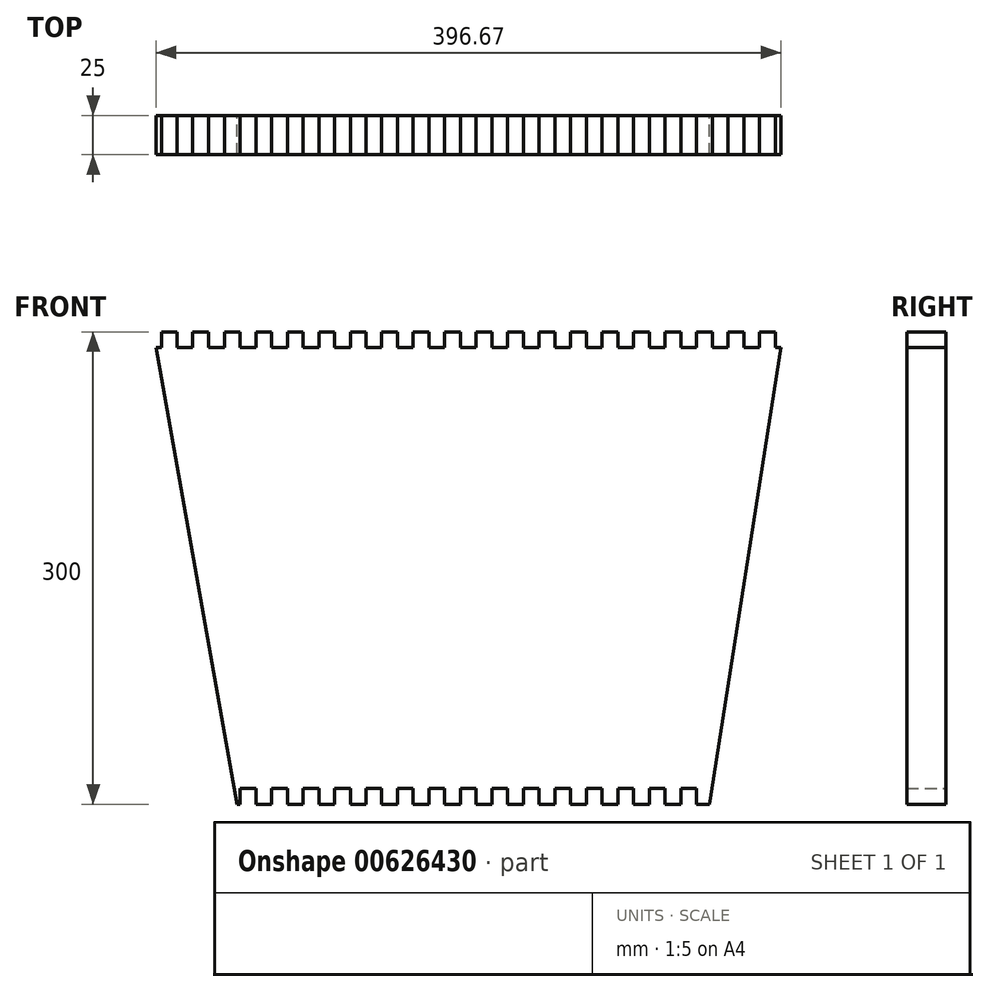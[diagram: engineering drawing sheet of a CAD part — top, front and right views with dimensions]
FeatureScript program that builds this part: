
annotation { "Feature Type Name" : "Feature", "Feature Type Description" : "" }
export const myFeature = defineFeature(function(context is Context, id is Id, definition is map)
    precondition{}
    {
        {
            var Q0;
            Q0=qCreatedBy(makeId("Front.planeOp"),FACE);
            var sketch = newSketch(context, id + "F0", { "sketchPlane" : qUnion([Q0])});
            skLineSegment(sketch, "E0.top", {"start": v(200, 150) * mm, "end": v(-200, 150) * mm});
            skPoint(sketch, "E0.middle", {"position": v(0, 0) * mm});
            skLineSegment(sketch, "E1.bottom", {"start": v(153.17, -150) * mm, "end": v(-146.83, -150) * mm});
            skLineSegment(sketch, "E2", {"start": v(-200, 150) * mm, "end": v(-146.83, -150) * mm});
            skLineSegment(sketch, "E3", {"start": v(153.17, -150) * mm, "end": v(200, 150) * mm});
            skLineSegment(sketch, "E4", {"start": v(5, 150) * mm, "end": v(0, 150) * mm});
            skLineSegment(sketch, "E5.bottom", {"start": v(5, 150) * mm, "end": v(-5, 150) * mm});
            skLineSegment(sketch, "E5.top", {"start": v(5, 140) * mm, "end": v(-5, 140) * mm});
            skLineSegment(sketch, "E5.left", {"start": v(5, 150) * mm, "end": v(5, 140) * mm});
            skLineSegment(sketch, "E5.right", {"start": v(-5, 150) * mm, "end": v(-5, 140) * mm});
            skLineSegment(sketch, "E6.1.0.0", {"start": v(-25, 150) * mm, "end": v(-25, 140) * mm});
            skLineSegment(sketch, "E6.1.0.1", {"start": v(-15, 140) * mm, "end": v(-25, 140) * mm});
            skLineSegment(sketch, "E6.1.0.2", {"start": v(-15, 150) * mm, "end": v(-15, 140) * mm});
            skLineSegment(sketch, "E6.1.0.3", {"start": v(-15, 150) * mm, "end": v(-25, 150) * mm});
            skLineSegment(sketch, "E6.2.0.0", {"start": v(-45, 150) * mm, "end": v(-45, 140) * mm});
            skLineSegment(sketch, "E6.2.0.1", {"start": v(-35, 140) * mm, "end": v(-45, 140) * mm});
            skLineSegment(sketch, "E6.2.0.2", {"start": v(-35, 150) * mm, "end": v(-35, 140) * mm});
            skLineSegment(sketch, "E6.2.0.3", {"start": v(-35, 150) * mm, "end": v(-45, 150) * mm});
            skLineSegment(sketch, "E6.3.0.0", {"start": v(-65, 150) * mm, "end": v(-65, 140) * mm});
            skLineSegment(sketch, "E6.3.0.1", {"start": v(-55, 140) * mm, "end": v(-65, 140) * mm});
            skLineSegment(sketch, "E6.3.0.2", {"start": v(-55, 150) * mm, "end": v(-55, 140) * mm});
            skLineSegment(sketch, "E6.3.0.3", {"start": v(-55, 150) * mm, "end": v(-65, 150) * mm});
            skLineSegment(sketch, "E6.4.0.0", {"start": v(-85, 150) * mm, "end": v(-85, 140) * mm});
            skLineSegment(sketch, "E6.4.0.1", {"start": v(-75, 140) * mm, "end": v(-85, 140) * mm});
            skLineSegment(sketch, "E6.4.0.2", {"start": v(-75, 150) * mm, "end": v(-75, 140) * mm});
            skLineSegment(sketch, "E6.4.0.3", {"start": v(-75, 150) * mm, "end": v(-85, 150) * mm});
            skLineSegment(sketch, "E6.5.0.0", {"start": v(-105, 150) * mm, "end": v(-105, 140) * mm});
            skLineSegment(sketch, "E6.5.0.1", {"start": v(-95, 140) * mm, "end": v(-105, 140) * mm});
            skLineSegment(sketch, "E6.5.0.2", {"start": v(-95, 150) * mm, "end": v(-95, 140) * mm});
            skLineSegment(sketch, "E6.5.0.3", {"start": v(-95, 150) * mm, "end": v(-105, 150) * mm});
            skLineSegment(sketch, "E6.6.0.0", {"start": v(-125, 150) * mm, "end": v(-125, 140) * mm});
            skLineSegment(sketch, "E6.6.0.1", {"start": v(-115, 140) * mm, "end": v(-125, 140) * mm});
            skLineSegment(sketch, "E6.6.0.2", {"start": v(-115, 150) * mm, "end": v(-115, 140) * mm});
            skLineSegment(sketch, "E6.6.0.3", {"start": v(-115, 150) * mm, "end": v(-125, 150) * mm});
            skLineSegment(sketch, "E6.7.0.0", {"start": v(-145, 150) * mm, "end": v(-145, 140) * mm});
            skLineSegment(sketch, "E6.7.0.1", {"start": v(-135, 140) * mm, "end": v(-145, 140) * mm});
            skLineSegment(sketch, "E6.7.0.2", {"start": v(-135, 150) * mm, "end": v(-135, 140) * mm});
            skLineSegment(sketch, "E6.7.0.3", {"start": v(-135, 150) * mm, "end": v(-145, 150) * mm});
            skLineSegment(sketch, "E6.8.0.0", {"start": v(-165, 150) * mm, "end": v(-165, 140) * mm});
            skLineSegment(sketch, "E6.8.0.1", {"start": v(-155, 140) * mm, "end": v(-165, 140) * mm});
            skLineSegment(sketch, "E6.8.0.2", {"start": v(-155, 150) * mm, "end": v(-155, 140) * mm});
            skLineSegment(sketch, "E6.8.0.3", {"start": v(-155, 150) * mm, "end": v(-165, 150) * mm});
            skLineSegment(sketch, "E6.9.0.0", {"start": v(-185, 150) * mm, "end": v(-185, 140) * mm});
            skLineSegment(sketch, "E6.9.0.1", {"start": v(-175, 140) * mm, "end": v(-185, 140) * mm});
            skLineSegment(sketch, "E6.9.0.2", {"start": v(-175, 150) * mm, "end": v(-175, 140) * mm});
            skLineSegment(sketch, "E6.9.0.3", {"start": v(-175, 150) * mm, "end": v(-185, 150) * mm});
            skLineSegment(sketch, "E6.10.0.0", {"start": v(-205, 150) * mm, "end": v(-205, 140) * mm});
            skLineSegment(sketch, "E6.10.0.1", {"start": v(-195, 140) * mm, "end": v(-205, 140) * mm});
            skLineSegment(sketch, "E6.10.0.2", {"start": v(-195, 150) * mm, "end": v(-195, 140) * mm});
            skLineSegment(sketch, "E6.10.0.3", {"start": v(-195, 150) * mm, "end": v(-205, 150) * mm});
            skLineSegment(sketch, "E7.1.0.0", {"start": v(15, 150) * mm, "end": v(15, 140) * mm});
            skLineSegment(sketch, "E7.1.0.1", {"start": v(25, 140) * mm, "end": v(15, 140) * mm});
            skLineSegment(sketch, "E7.1.0.2", {"start": v(25, 150) * mm, "end": v(25, 140) * mm});
            skLineSegment(sketch, "E7.1.0.3", {"start": v(25, 150) * mm, "end": v(15, 150) * mm});
            skLineSegment(sketch, "E7.2.0.0", {"start": v(35, 150) * mm, "end": v(35, 140) * mm});
            skLineSegment(sketch, "E7.2.0.1", {"start": v(45, 140) * mm, "end": v(35, 140) * mm});
            skLineSegment(sketch, "E7.2.0.2", {"start": v(45, 150) * mm, "end": v(45, 140) * mm});
            skLineSegment(sketch, "E7.2.0.3", {"start": v(45, 150) * mm, "end": v(35, 150) * mm});
            skLineSegment(sketch, "E7.3.0.0", {"start": v(55, 150) * mm, "end": v(55, 140) * mm});
            skLineSegment(sketch, "E7.3.0.1", {"start": v(65, 140) * mm, "end": v(55, 140) * mm});
            skLineSegment(sketch, "E7.3.0.2", {"start": v(65, 150) * mm, "end": v(65, 140) * mm});
            skLineSegment(sketch, "E7.3.0.3", {"start": v(65, 150) * mm, "end": v(55, 150) * mm});
            skLineSegment(sketch, "E7.4.0.0", {"start": v(75, 150) * mm, "end": v(75, 140) * mm});
            skLineSegment(sketch, "E7.4.0.1", {"start": v(85, 140) * mm, "end": v(75, 140) * mm});
            skLineSegment(sketch, "E7.4.0.2", {"start": v(85, 150) * mm, "end": v(85, 140) * mm});
            skLineSegment(sketch, "E7.4.0.3", {"start": v(85, 150) * mm, "end": v(75, 150) * mm});
            skLineSegment(sketch, "E7.5.0.0", {"start": v(95, 150) * mm, "end": v(95, 140) * mm});
            skLineSegment(sketch, "E7.5.0.1", {"start": v(105, 140) * mm, "end": v(95, 140) * mm});
            skLineSegment(sketch, "E7.5.0.2", {"start": v(105, 150) * mm, "end": v(105, 140) * mm});
            skLineSegment(sketch, "E7.5.0.3", {"start": v(105, 150) * mm, "end": v(95, 150) * mm});
            skLineSegment(sketch, "E7.6.0.0", {"start": v(115, 150) * mm, "end": v(115, 140) * mm});
            skLineSegment(sketch, "E7.6.0.1", {"start": v(125, 140) * mm, "end": v(115, 140) * mm});
            skLineSegment(sketch, "E7.6.0.2", {"start": v(125, 150) * mm, "end": v(125, 140) * mm});
            skLineSegment(sketch, "E7.6.0.3", {"start": v(125, 150) * mm, "end": v(115, 150) * mm});
            skLineSegment(sketch, "E7.7.0.0", {"start": v(135, 150) * mm, "end": v(135, 140) * mm});
            skLineSegment(sketch, "E7.7.0.1", {"start": v(145, 140) * mm, "end": v(135, 140) * mm});
            skLineSegment(sketch, "E7.7.0.2", {"start": v(145, 150) * mm, "end": v(145, 140) * mm});
            skLineSegment(sketch, "E7.7.0.3", {"start": v(145, 150) * mm, "end": v(135, 150) * mm});
            skLineSegment(sketch, "E7.8.0.0", {"start": v(155, 150) * mm, "end": v(155, 140) * mm});
            skLineSegment(sketch, "E7.8.0.1", {"start": v(165, 140) * mm, "end": v(155, 140) * mm});
            skLineSegment(sketch, "E7.8.0.2", {"start": v(165, 150) * mm, "end": v(165, 140) * mm});
            skLineSegment(sketch, "E7.8.0.3", {"start": v(165, 150) * mm, "end": v(155, 150) * mm});
            skLineSegment(sketch, "E7.9.0.0", {"start": v(175, 150) * mm, "end": v(175, 140) * mm});
            skLineSegment(sketch, "E7.9.0.1", {"start": v(185, 140) * mm, "end": v(175, 140) * mm});
            skLineSegment(sketch, "E7.9.0.2", {"start": v(185, 150) * mm, "end": v(185, 140) * mm});
            skLineSegment(sketch, "E7.9.0.3", {"start": v(185, 150) * mm, "end": v(175, 150) * mm});
            skLineSegment(sketch, "E7.10.0.0", {"start": v(195, 150) * mm, "end": v(195, 140) * mm});
            skLineSegment(sketch, "E7.10.0.1", {"start": v(205, 140) * mm, "end": v(195, 140) * mm});
            skLineSegment(sketch, "E7.10.0.2", {"start": v(205, 150) * mm, "end": v(205, 140) * mm});
            skLineSegment(sketch, "E7.10.0.3", {"start": v(205, 150) * mm, "end": v(195, 150) * mm});
            skLineSegment(sketch, "E7.direction1", {"start": v(-5, 140) * mm, "end": v(15, 140) * mm, "construction": true});
            skLineSegment(sketch, "E8.MirrorCS", {"start": v(95, -150) * mm, "end": v(95, -140) * mm});
            skLineSegment(sketch, "E9.MirrorCS", {"start": v(15, -150) * mm, "end": v(15, -140) * mm});
            skLineSegment(sketch, "E10.MirrorCS", {"start": v(105, -140) * mm, "end": v(95, -140) * mm});
            skLineSegment(sketch, "E11.MirrorCS", {"start": v(25, -140) * mm, "end": v(15, -140) * mm});
            skLineSegment(sketch, "E12.MirrorCS", {"start": v(195, -150) * mm, "end": v(195, -140) * mm});
            skLineSegment(sketch, "E13.MirrorCS", {"start": v(45, -150) * mm, "end": v(45, -140) * mm});
            skLineSegment(sketch, "E14.MirrorCS", {"start": v(-155, -150) * mm, "end": v(-155, -140) * mm});
            skLineSegment(sketch, "E15.MirrorCS", {"start": v(-75, -150) * mm, "end": v(-75, -140) * mm});
            skLineSegment(sketch, "E16.MirrorCS", {"start": v(125, -150) * mm, "end": v(125, -140) * mm});
            skLineSegment(sketch, "E17.MirrorCS", {"start": v(-5, -150) * mm, "end": v(-5, -140) * mm});
            skLineSegment(sketch, "E18.MirrorCS", {"start": v(-45, -150) * mm, "end": v(-45, -140) * mm});
            skLineSegment(sketch, "E19.MirrorCS", {"start": v(-15, -150) * mm, "end": v(-25, -150) * mm});
            skLineSegment(sketch, "E20.MirrorCS", {"start": v(-125, -150) * mm, "end": v(-125, -140) * mm});
            skLineSegment(sketch, "E21.MirrorCS", {"start": v(5, -140) * mm, "end": v(-5, -140) * mm});
            skLineSegment(sketch, "E22.MirrorCS", {"start": v(-5, -140) * mm, "end": v(15, -140) * mm, "construction": true});
            skLineSegment(sketch, "E23.MirrorCS", {"start": v(155, -150) * mm, "end": v(155, -140) * mm});
            skLineSegment(sketch, "E24.MirrorCS", {"start": v(-185, -150) * mm, "end": v(-185, -140) * mm});
            skLineSegment(sketch, "E25.MirrorCS", {"start": v(5, -150) * mm, "end": v(0, -150) * mm});
            skLineSegment(sketch, "E26.MirrorCS", {"start": v(5, -150) * mm, "end": v(-5, -150) * mm});
            skLineSegment(sketch, "E27.MirrorCS", {"start": v(85, -150) * mm, "end": v(75, -150) * mm});
            skLineSegment(sketch, "E28.MirrorCS", {"start": v(-195, -150) * mm, "end": v(-205, -150) * mm});
            skLineSegment(sketch, "E29.MirrorCS", {"start": v(-115, -150) * mm, "end": v(-125, -150) * mm});
            skLineSegment(sketch, "E30.MirrorCS", {"start": v(-65, -150) * mm, "end": v(-65, -140) * mm});
            skLineSegment(sketch, "E31.MirrorCS", {"start": v(175, -150) * mm, "end": v(175, -140) * mm});
            skLineSegment(sketch, "E32.MirrorCS", {"start": v(-145, -150) * mm, "end": v(-145, -140) * mm});
            skLineSegment(sketch, "E33.MirrorCS", {"start": v(-55, -140) * mm, "end": v(-65, -140) * mm});
            skLineSegment(sketch, "E34.MirrorCS", {"start": v(185, -140) * mm, "end": v(175, -140) * mm});
            skLineSegment(sketch, "E35.MirrorCS", {"start": v(-135, -140) * mm, "end": v(-145, -140) * mm});
            skLineSegment(sketch, "E36.MirrorCS", {"start": v(-55, -150) * mm, "end": v(-55, -140) * mm});
            skLineSegment(sketch, "E37.MirrorCS", {"start": v(185, -150) * mm, "end": v(185, -140) * mm});
            skLineSegment(sketch, "E38.MirrorCS", {"start": v(105, -150) * mm, "end": v(105, -140) * mm});
            skLineSegment(sketch, "E39.MirrorCS", {"start": v(25, -150) * mm, "end": v(25, -140) * mm});
            skLineSegment(sketch, "E40.MirrorCS", {"start": v(-135, -150) * mm, "end": v(-135, -140) * mm});
            skLineSegment(sketch, "E41.MirrorCS", {"start": v(-55, -150) * mm, "end": v(-65, -150) * mm});
            skLineSegment(sketch, "E42.MirrorCS", {"start": v(185, -150) * mm, "end": v(175, -150) * mm});
            skLineSegment(sketch, "E43.MirrorCS", {"start": v(105, -150) * mm, "end": v(95, -150) * mm});
            skLineSegment(sketch, "E44.MirrorCS", {"start": v(25, -150) * mm, "end": v(15, -150) * mm});
            skLineSegment(sketch, "E45.MirrorCS", {"start": v(-135, -150) * mm, "end": v(-145, -150) * mm});
            skLineSegment(sketch, "E46.MirrorCS", {"start": v(35, -150) * mm, "end": v(35, -140) * mm});
            skLineSegment(sketch, "E47.MirrorCS", {"start": v(-165, -150) * mm, "end": v(-165, -140) * mm});
            skLineSegment(sketch, "E48.MirrorCS", {"start": v(-85, -150) * mm, "end": v(-85, -140) * mm});
            skLineSegment(sketch, "E49.MirrorCS", {"start": v(115, -150) * mm, "end": v(115, -140) * mm});
            skLineSegment(sketch, "E50.MirrorCS", {"start": v(45, -140) * mm, "end": v(35, -140) * mm});
            skLineSegment(sketch, "E51.MirrorCS", {"start": v(-155, -140) * mm, "end": v(-165, -140) * mm});
            skLineSegment(sketch, "E52.MirrorCS", {"start": v(-75, -140) * mm, "end": v(-85, -140) * mm});
            skLineSegment(sketch, "E53.MirrorCS", {"start": v(205, -140) * mm, "end": v(195, -140) * mm});
            skLineSegment(sketch, "E54.MirrorCS", {"start": v(125, -140) * mm, "end": v(115, -140) * mm});
            skLineSegment(sketch, "E55.MirrorCS", {"start": v(205, -150) * mm, "end": v(205, -140) * mm});
            skLineSegment(sketch, "E56.MirrorCS", {"start": v(45, -150) * mm, "end": v(35, -150) * mm});
            skLineSegment(sketch, "E57.MirrorCS", {"start": v(-75, -150) * mm, "end": v(-85, -150) * mm});
            skLineSegment(sketch, "E58.MirrorCS", {"start": v(-155, -150) * mm, "end": v(-165, -150) * mm});
            skLineSegment(sketch, "E59.MirrorCS", {"start": v(205, -150) * mm, "end": v(195, -150) * mm});
            skLineSegment(sketch, "E60.MirrorCS", {"start": v(125, -150) * mm, "end": v(115, -150) * mm});
            skLineSegment(sketch, "E61.MirrorCS", {"start": v(165, -150) * mm, "end": v(155, -150) * mm});
            skLineSegment(sketch, "E62.MirrorCS", {"start": v(-35, -150) * mm, "end": v(-45, -150) * mm});
            skLineSegment(sketch, "E63.MirrorCS", {"start": v(-95, -150) * mm, "end": v(-105, -150) * mm});
            skLineSegment(sketch, "E64.MirrorCS", {"start": v(-175, -150) * mm, "end": v(-185, -150) * mm});
            skLineSegment(sketch, "E65.MirrorCS", {"start": v(65, -150) * mm, "end": v(55, -150) * mm});
            skLineSegment(sketch, "E66.MirrorCS", {"start": v(-115, -150) * mm, "end": v(-115, -140) * mm});
            skLineSegment(sketch, "E67.MirrorCS", {"start": v(-195, -150) * mm, "end": v(-195, -140) * mm});
            skLineSegment(sketch, "E68.MirrorCS", {"start": v(85, -150) * mm, "end": v(85, -140) * mm});
            skLineSegment(sketch, "E69.MirrorCS", {"start": v(165, -150) * mm, "end": v(165, -140) * mm});
            skLineSegment(sketch, "E70.MirrorCS", {"start": v(145, -150) * mm, "end": v(135, -150) * mm});
            skLineSegment(sketch, "E71.MirrorCS", {"start": v(-35, -150) * mm, "end": v(-35, -140) * mm});
            skLineSegment(sketch, "E72.MirrorCS", {"start": v(145, -140) * mm, "end": v(135, -140) * mm});
            skLineSegment(sketch, "E73.MirrorCS", {"start": v(-95, -140) * mm, "end": v(-105, -140) * mm});
            skLineSegment(sketch, "E74.MirrorCS", {"start": v(-115, -140) * mm, "end": v(-125, -140) * mm});
            skLineSegment(sketch, "E75.MirrorCS", {"start": v(-195, -140) * mm, "end": v(-205, -140) * mm});
            skLineSegment(sketch, "E76.MirrorCS", {"start": v(85, -140) * mm, "end": v(75, -140) * mm});
            skLineSegment(sketch, "E77.MirrorCS", {"start": v(165, -140) * mm, "end": v(155, -140) * mm});
            skLineSegment(sketch, "E78.MirrorCS", {"start": v(-35, -140) * mm, "end": v(-45, -140) * mm});
            skLineSegment(sketch, "E79.MirrorCS", {"start": v(-15, -140) * mm, "end": v(-25, -140) * mm});
            skLineSegment(sketch, "E80.MirrorCS", {"start": v(-25, -150) * mm, "end": v(-25, -140) * mm});
            skLineSegment(sketch, "E81.MirrorCS", {"start": v(-175, -140) * mm, "end": v(-185, -140) * mm});
            skLineSegment(sketch, "E82.MirrorCS", {"start": v(65, -140) * mm, "end": v(55, -140) * mm});
            skLineSegment(sketch, "E83.MirrorCS", {"start": v(-95, -150) * mm, "end": v(-95, -140) * mm});
            skLineSegment(sketch, "E84.MirrorCS", {"start": v(-175, -150) * mm, "end": v(-175, -140) * mm});
            skLineSegment(sketch, "E85.MirrorCS", {"start": v(65, -150) * mm, "end": v(65, -140) * mm});
            skLineSegment(sketch, "E86.MirrorCS", {"start": v(200, -150) * mm, "end": v(-200, -150) * mm});
            skLineSegment(sketch, "E87.MirrorCS", {"start": v(145, -150) * mm, "end": v(145, -140) * mm});
            skLineSegment(sketch, "E88.MirrorCS", {"start": v(5, -150) * mm, "end": v(5, -140) * mm});
            skLineSegment(sketch, "E89.MirrorCS", {"start": v(-15, -150) * mm, "end": v(-15, -140) * mm});
            skLineSegment(sketch, "E90.MirrorCS", {"start": v(-205, -150) * mm, "end": v(-205, -140) * mm});
            skLineSegment(sketch, "E91.MirrorCS", {"start": v(75, -150) * mm, "end": v(75, -140) * mm});
            skLineSegment(sketch, "E92.MirrorCS", {"start": v(55, -150) * mm, "end": v(55, -140) * mm});
            skLineSegment(sketch, "E93.MirrorCS", {"start": v(135, -150) * mm, "end": v(135, -140) * mm});
            skLineSegment(sketch, "E94.MirrorCS", {"start": v(-105, -150) * mm, "end": v(-105, -140) * mm});
            skSolve(sketch);
        }
        {
            var Q0;
            Q0=makeQuery(id+"F0.imprint","IMPRINT",FACE,{"disambiguationData":[TD([[makeQuery(id+"F0.imprint","IMPRINT",EDGE,{"derivedFrom":sQuery(id+"F0.wireOp",EDGE,"E5.top")}),1.0]])]});
            extrude(context, id + "F1", {"entities" : qUnion([Q0]), "depth" : 25 * mm, "offsetDistance" : 25 * mm});
        }
    });
